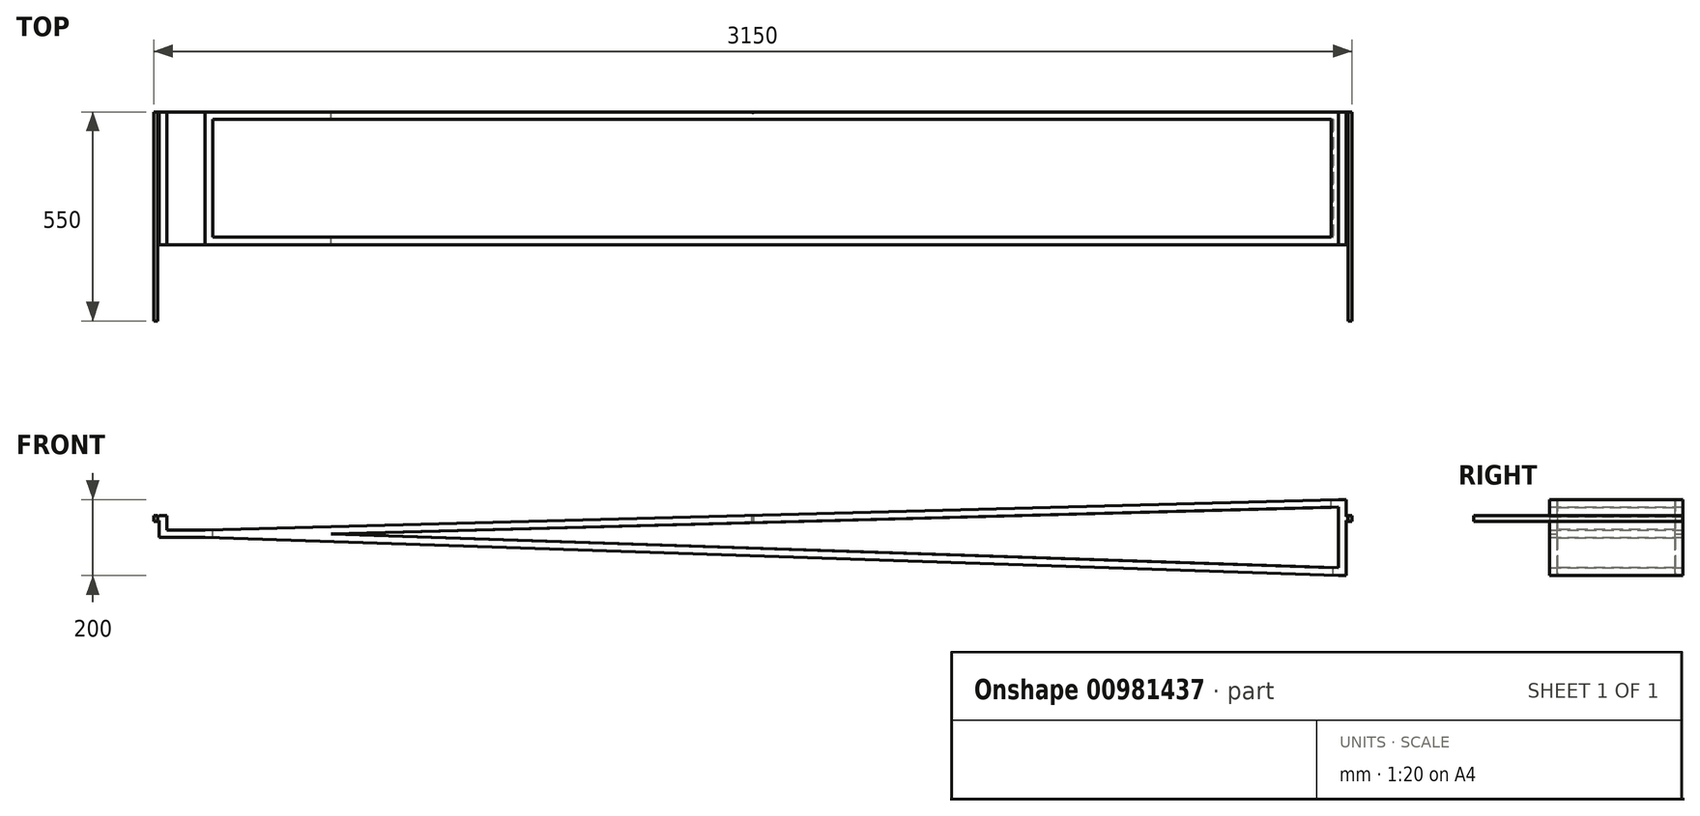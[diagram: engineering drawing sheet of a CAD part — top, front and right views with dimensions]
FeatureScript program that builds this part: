
annotation { "Feature Type Name" : "Feature", "Feature Type Description" : "" }
export const myFeature = defineFeature(function(context is Context, id is Id, definition is map)
    precondition{}
    {
        {
            var Q0;
            Q0=qCreatedBy(makeId("Front.planeOp"),FACE);
            var sketch = newSketch(context, id + "F0", { "sketchPlane" : qUnion([Q0])});
            skLineSegment(sketch, "E0", {"start": v(-10, 30) * mm, "end": v(-10, -130) * mm});
            skLineSegment(sketch, "E1", {"start": v(-10, -150) * mm, "end": v(10, -150) * mm});
            skLineSegment(sketch, "E2", {"start": v(10, -150) * mm, "end": v(10, -5) * mm});
            skLineSegment(sketch, "E3", {"start": v(10, 50) * mm, "end": v(-10, 50) * mm});
            skLineSegment(sketch, "E4", {"start": v(25, -7.5) * mm, "end": v(25, 7.5) * mm});
            skLineSegment(sketch, "E5", {"start": v(25, 7.5) * mm, "end": v(15, 7.5) * mm});
            skLineSegment(sketch, "E6", {"start": v(15, 7.5) * mm, "end": v(15, 5) * mm});
            skLineSegment(sketch, "E7", {"start": v(15, 5) * mm, "end": v(10, 5) * mm});
            skLineSegment(sketch, "E8", {"start": v(25, -7.5) * mm, "end": v(15, -7.5) * mm});
            skLineSegment(sketch, "E9", {"start": v(15, -7.5) * mm, "end": v(15, -5) * mm});
            skLineSegment(sketch, "E10", {"start": v(15, -5) * mm, "end": v(10, -5) * mm});
            skLineSegment(sketch, "E11.trimOffspring", {"start": v(10, 5) * mm, "end": v(10, 50) * mm});
            skLineSegment(sketch, "E12.MirrorCS", {"start": v(-3115, 7.5) * mm, "end": v(-3115, 5) * mm});
            skLineSegment(sketch, "E13.MirrorCS", {"start": v(-3115, -7.5) * mm, "end": v(-3115, -5) * mm});
            skLineSegment(sketch, "E14.MirrorCS", {"start": v(-3115, 5) * mm, "end": v(-3110, 5) * mm});
            skLineSegment(sketch, "E15.MirrorCS", {"start": v(-3115, -5) * mm, "end": v(-3110, -5) * mm});
            skLineSegment(sketch, "E16.MirrorCS", {"start": v(-3125, -7.5) * mm, "end": v(-3115, -7.5) * mm});
            skLineSegment(sketch, "E17.MirrorCS", {"start": v(-3125, -7.5) * mm, "end": v(-3125, 7.5) * mm});
            skLineSegment(sketch, "E18.MirrorCS", {"start": v(-3125, 7.5) * mm, "end": v(-3115, 7.5) * mm});
            skLineSegment(sketch, "E19.MirrorCS", {"start": v(-3110, 5) * mm, "end": v(-3110, 7.5) * mm});
            skLineSegment(sketch, "E20.MirrorCS", {"start": v(-3090, 7.5) * mm, "end": v(-3090, -30) * mm});
            skLineSegment(sketch, "E21.MirrorCS", {"start": v(-3110, -50) * mm, "end": v(-3110, -5) * mm});
            skLineSegment(sketch, "E22", {"start": v(-3110, 7.5) * mm, "end": v(-3090, 7.5) * mm});
            skLineSegment(sketch, "E23", {"start": v(-3090, -30) * mm, "end": v(-2990, -30) * mm});
            skLineSegment(sketch, "E24", {"start": v(-2990, -50) * mm, "end": v(-3110, -50) * mm});
            skPoint(sketch, "E25", {"position": v(-10, -130) * mm});
            skPoint(sketch, "E26", {"position": v(-10, 30) * mm});
            skLineSegment(sketch, "E27", {"start": v(-10, -150) * mm, "end": v(-2990, -50) * mm});
            skLineSegment(sketch, "E28", {"start": v(-2658.89, -41.11) * mm, "end": v(-10, -130) * mm});
            skLineSegment(sketch, "E29", {"start": v(-10, 30) * mm, "end": v(-2658.89, -41.11) * mm});
            skLineSegment(sketch, "E30", {"start": v(-2990, -30) * mm, "end": v(-10, 50) * mm});
            skSolve(sketch);
        }
        {
            var Q0;
            Q0=makeQuery(id+"F0.imprint","IMPRINT",FACE,{"disambiguationData":[TD([[makeQuery(id+"F0.imprint","IMPRINT",EDGE,{"derivedFrom":sQuery(id+"F0.wireOp",EDGE,"E0")}),1.0]])]});
            extrude(context, id + "F1", {"entities" : qUnion([Q0]), "depth" : 350 * mm, "offsetDistance" : 25 * mm});
        }
        {
            var Q0;
            Q0=makeQuery(id+"F1.opExtrude","SWEPT_FACE",FACE,{"disambiguationData":[OSD([sQuery(id+"F0.wireOp",EDGE,"E30")])]});
            cPlane(context, id + "F2", {"entities" : qUnion([Q0]), "cplaneType" : CPlaneType.OFFSET, "offset" : 0 * mm, "width" : 150 * mm, "height" : 150 * mm});
        }
        {
            var Q0;
            Q0=qCreatedBy(id+"F2.planeOp",FACE);
            var sketch = newSketch(context, id + "F3", { "sketchPlane" : qUnion([Q0])});
            skLineSegment(sketch, "E31.bottom", {"start": v(-8.66, 0) * mm, "end": v(-2989.73, 0) * mm});
            skLineSegment(sketch, "E31.top", {"start": v(-8.66, -350) * mm, "end": v(-2989.73, -350) * mm});
            skLineSegment(sketch, "E31.left", {"start": v(-8.66, 0) * mm, "end": v(-8.66, -350) * mm});
            skLineSegment(sketch, "E31.right", {"start": v(-2989.73, 0) * mm, "end": v(-2989.73, -350) * mm});
            skLineSegment(sketch, "E32.0", {"start": v(-28.66, -20) * mm, "end": v(-2969.73, -20) * mm});
            skLineSegment(sketch, "E32.1", {"start": v(-28.66, -20) * mm, "end": v(-28.66, -330) * mm});
            skLineSegment(sketch, "E32.2", {"start": v(-28.66, -330) * mm, "end": v(-2969.73, -330) * mm});
            skLineSegment(sketch, "E32.3", {"start": v(-2969.73, -20) * mm, "end": v(-2969.73, -330) * mm});
            skSolve(sketch);
        }
        {
            var Q0;
            Q0=makeQuery(id+"F3.imprint","IMPRINT",FACE,{"disambiguationData":[TD([[makeQuery(id+"F3.imprint","IMPRINT",EDGE,{"derivedFrom":sQuery(id+"F3.wireOp",EDGE,"E32.0")}),1.0]])]});
            extrude(context, id + "F4", {"entities" : qUnion([Q0]), "operationType" : NewBodyOperationType.REMOVE, "oppositeDirection" : true, "depth" : 250 * mm, "offsetDistance" : 25 * mm});
        }
        {
            var Q0;
            Q0=makeQuery(id+"F1.opExtrude","CAP_FACE",FACE,{"disambiguationData":[OSD([sQuery(id+"F0.wireOp",EDGE,"E0"),sQuery(id+"F0.wireOp",EDGE,"E1"),sQuery(id+"F0.wireOp",EDGE,"E2"),sQuery(id+"F0.wireOp",EDGE,"E3"),sQuery(id+"F0.wireOp",EDGE,"E4"),sQuery(id+"F0.wireOp",EDGE,"E5"),sQuery(id+"F0.wireOp",EDGE,"E6"),sQuery(id+"F0.wireOp",EDGE,"E7"),sQuery(id+"F0.wireOp",EDGE,"E8"),sQuery(id+"F0.wireOp",EDGE,"E9"),sQuery(id+"F0.wireOp",EDGE,"E10"),sQuery(id+"F0.wireOp",EDGE,"E11.trimOffspring"),sQuery(id+"F0.wireOp",EDGE,"E12.MirrorCS"),sQuery(id+"F0.wireOp",EDGE,"E13.MirrorCS"),sQuery(id+"F0.wireOp",EDGE,"E14.MirrorCS"),sQuery(id+"F0.wireOp",EDGE,"E15.MirrorCS"),sQuery(id+"F0.wireOp",EDGE,"E16.MirrorCS"),sQuery(id+"F0.wireOp",EDGE,"E17.MirrorCS"),sQuery(id+"F0.wireOp",EDGE,"E18.MirrorCS"),sQuery(id+"F0.wireOp",EDGE,"E19.MirrorCS"),sQuery(id+"F0.wireOp",EDGE,"E20.MirrorCS"),sQuery(id+"F0.wireOp",EDGE,"E21.MirrorCS"),sQuery(id+"F0.wireOp",EDGE,"E22"),sQuery(id+"F0.wireOp",EDGE,"E23"),sQuery(id+"F0.wireOp",EDGE,"E24"),sQuery(id+"F0.wireOp",EDGE,"E27"),sQuery(id+"F0.wireOp",EDGE,"E28"),sQuery(id+"F0.wireOp",EDGE,"E29"),sQuery(id+"F0.wireOp",EDGE,"E30")])],"isStart":false});
            cPlane(context, id + "F5", {"entities" : qUnion([Q0]), "cplaneType" : CPlaneType.OFFSET, "offset" : 0 * mm, "width" : 150 * mm, "height" : 150 * mm});
        }
        {
            var Q0;
            Q0=qCreatedBy(id+"F5.planeOp",FACE);
            var sketch = newSketch(context, id + "F6", { "sketchPlane" : qUnion([Q0])});
            skLineSegment(sketch, "E33", {"start": v(15, 7.5) * mm, "end": v(25, 7.5) * mm});
            skLineSegment(sketch, "E34", {"start": v(25, 7.5) * mm, "end": v(25, -7.5) * mm});
            skLineSegment(sketch, "E35", {"start": v(15, 7.5) * mm, "end": v(15, -7.5) * mm});
            skLineSegment(sketch, "E36", {"start": v(15, -7.5) * mm, "end": v(25, -7.5) * mm});
            skLineSegment(sketch, "E37", {"start": v(-3125, 7.5) * mm, "end": v(-3125, -7.5) * mm});
            skLineSegment(sketch, "E38", {"start": v(-3125, -7.5) * mm, "end": v(-3115, -7.5) * mm});
            skLineSegment(sketch, "E39", {"start": v(-3115, -7.5) * mm, "end": v(-3115, 7.5) * mm});
            skLineSegment(sketch, "E40", {"start": v(-3115, 7.5) * mm, "end": v(-3125, 7.5) * mm});
            skSolve(sketch);
        }
        {
            var Q0;
            Q0 = qSketchRegion(id + "F6", true);
            extrude(context, id + "F7", {"entities" : qUnion([Q0]), "operationType" : NewBodyOperationType.ADD, "depth" : 200 * mm, "offsetDistance" : 25 * mm});
        }
        {
            var Q0;
            Q0=makeQuery(id+"F1.opExtrude","SWEPT_FACE",FACE,{"disambiguationData":[OSD([sQuery(id+"F0.wireOp",EDGE,"E30")])]});
            cPlane(context, id + "F8", {"entities" : qUnion([Q0]), "cplaneType" : CPlaneType.OFFSET, "offset" : 0 * mm, "width" : 150 * mm, "height" : 150 * mm});
        }
        {
            var Q0;
            Q0=qCreatedBy(id+"F8.planeOp",FACE);
            var sketch = newSketch(context, id + "F9", { "sketchPlane" : qUnion([Q0])});
            skPoint(sketch, "E41", {"position": v(-1549.2, 0) * mm});
            skSolve(sketch);
        }
        {
            var Q0;
            Q0=sQuery(id+"F9.wireOp",VERTEX,"E41");
            var Q1;
            Q1=makeQuery(id+"F1.opExtrude","SWEPT_BODY",BODY,{"disambiguationData":[OSD([sQuery(id+"F0.wireOp",EDGE,"E0"),sQuery(id+"F0.wireOp",EDGE,"E1"),sQuery(id+"F0.wireOp",EDGE,"E2"),sQuery(id+"F0.wireOp",EDGE,"E3"),sQuery(id+"F0.wireOp",EDGE,"E4"),sQuery(id+"F0.wireOp",EDGE,"E5"),sQuery(id+"F0.wireOp",EDGE,"E6"),sQuery(id+"F0.wireOp",EDGE,"E7"),sQuery(id+"F0.wireOp",EDGE,"E8"),sQuery(id+"F0.wireOp",EDGE,"E9"),sQuery(id+"F0.wireOp",EDGE,"E10"),sQuery(id+"F0.wireOp",EDGE,"E11.trimOffspring"),sQuery(id+"F0.wireOp",EDGE,"E12.MirrorCS"),sQuery(id+"F0.wireOp",EDGE,"E13.MirrorCS"),sQuery(id+"F0.wireOp",EDGE,"E14.MirrorCS"),sQuery(id+"F0.wireOp",EDGE,"E15.MirrorCS"),sQuery(id+"F0.wireOp",EDGE,"E16.MirrorCS"),sQuery(id+"F0.wireOp",EDGE,"E17.MirrorCS"),sQuery(id+"F0.wireOp",EDGE,"E18.MirrorCS"),sQuery(id+"F0.wireOp",EDGE,"E19.MirrorCS"),sQuery(id+"F0.wireOp",EDGE,"E20.MirrorCS"),sQuery(id+"F0.wireOp",EDGE,"E21.MirrorCS"),sQuery(id+"F0.wireOp",EDGE,"E22"),sQuery(id+"F0.wireOp",EDGE,"E23"),sQuery(id+"F0.wireOp",EDGE,"E24"),sQuery(id+"F0.wireOp",EDGE,"E27"),sQuery(id+"F0.wireOp",EDGE,"E28"),sQuery(id+"F0.wireOp",EDGE,"E29"),sQuery(id+"F0.wireOp",EDGE,"E30")])]});
            hole(context, id + "F10", {"style" : HoleStyle.SIMPLE, "endStyle" : HoleEndStyle.BLIND, "holeDiameter" : 5 * mm, "majorDiameter" : 5 * mm, "holeDepth" : 50 * mm, "isTappedThrough" : true, "tappedDepth" : 12 * mm, "tapClearance" : 3, "startFromSketch" : true, "locations" : qUnion([Q0]), "scope" : qUnion([Q1])});
        }
    });
